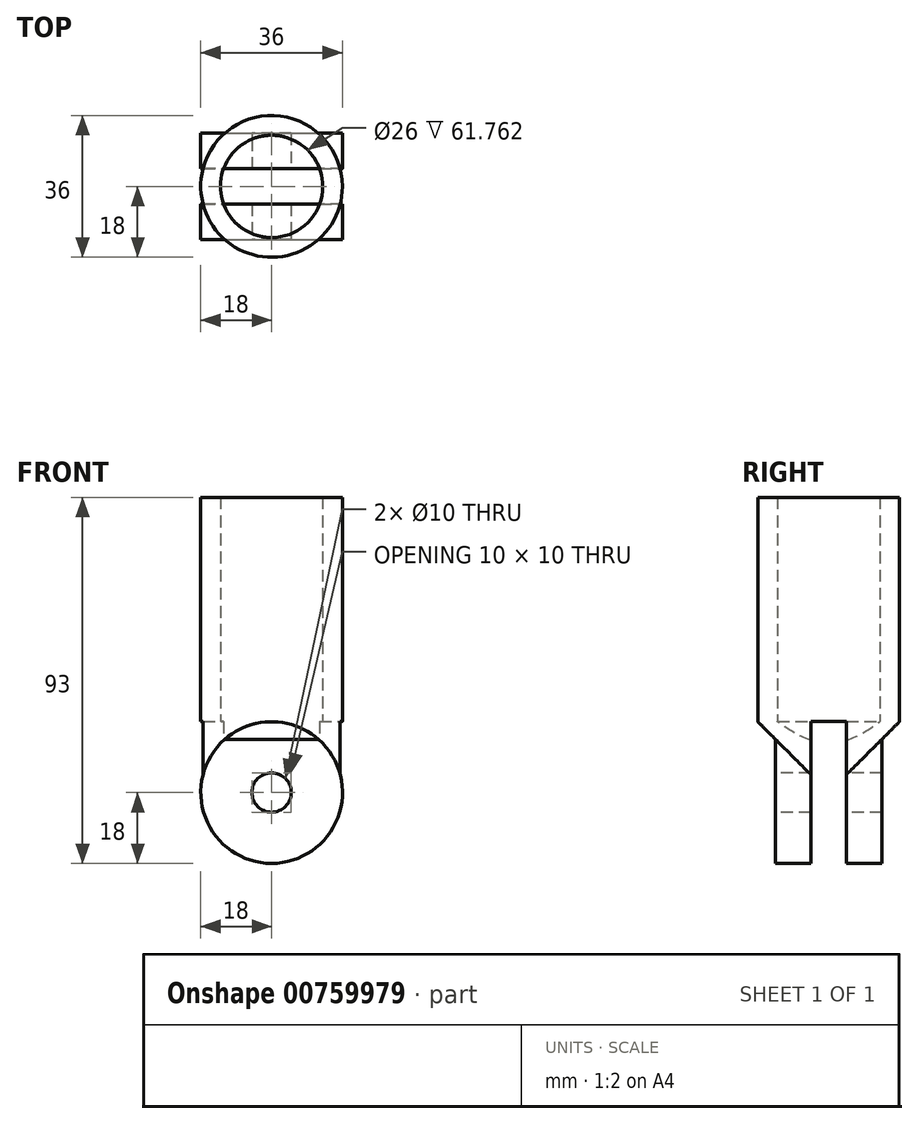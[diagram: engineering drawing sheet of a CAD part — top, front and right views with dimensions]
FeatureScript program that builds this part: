
annotation { "Feature Type Name" : "Feature", "Feature Type Description" : "" }
export const myFeature = defineFeature(function(context is Context, id is Id, definition is map)
    precondition{}
    {
        {
            var Q0;
            Q0=qCreatedBy(makeId("Top.planeOp"),FACE);
            var sketch = newSketch(context, id + "F0", { "sketchPlane" : qUnion([Q0])});
            skCircle(sketch, "E0", {"center": v(0, 0) * mm, "radius": 18 * mm});
            skCircle(sketch, "E1", {"center": v(0, 0) * mm, "radius": 13 * mm});
            skSolve(sketch);
        }
        {
            var Q0;
            Q0 = qSketchRegion(id + "F0", true);
            extrude(context, id + "F1", {"entities" : qUnion([Q0]), "depth" : 75 * mm, "offsetDistance" : 25 * mm});
        }
        {
            var Q0;
            Q0=qCreatedBy(makeId("Front.planeOp"),FACE);
            var sketch = newSketch(context, id + "F2", { "sketchPlane" : qUnion([Q0])});
            skCircle(sketch, "E2", {"center": v(0, 0) * mm, "radius": 18 * mm});
            skSolve(sketch);
        }
        {
            var Q0;
            Q0=makeQuery(id+"F2.imprint","IMPRINT",FACE,{"disambiguationData":[TD([[makeQuery(id+"F2.imprint","IMPRINT",EDGE,{"derivedFrom":sQuery(id+"F2.wireOp",EDGE,"E2")}),1.0]])]});
            extrude(context, id + "F3", {"entities" : qUnion([Q0]), "operationType" : NewBodyOperationType.ADD, "endBound" : BoundingType.SYMMETRIC, "depth" : (9 * 3) * mm, "offsetDistance" : 25 * mm});
        }
        {
            var Q0;
            Q0=qCreatedBy(makeId("Right.planeOp"),FACE);
            var sketch = newSketch(context, id + "F4", { "sketchPlane" : qUnion([Q0])});
            skLineSegment(sketch, "E3.bottom", {"start": v(4.5, -18) * mm, "end": v(-4.5, -18) * mm});
            skLineSegment(sketch, "E3.top", {"start": v(4.5, 18) * mm, "end": v(-4.5, 18) * mm});
            skLineSegment(sketch, "E3.left", {"start": v(4.5, -18) * mm, "end": v(4.5, 18) * mm});
            skLineSegment(sketch, "E3.right", {"start": v(-4.5, -18) * mm, "end": v(-4.5, 18) * mm});
            skPoint(sketch, "E3.middle", {"position": v(0, 0) * mm});
            skSolve(sketch);
        }
        {
            var Q0;
            Q0 = qSketchRegion(id + "F4", true);
            extrude(context, id + "F5", {"entities" : qUnion([Q0]), "operationType" : NewBodyOperationType.REMOVE, "endBound" : BoundingType.SYMMETRIC, "oppositeDirection" : true, "depth" : 40 * mm, "offsetDistance" : 25 * mm});
        }
        {
            var Q0;
            Q0=qCreatedBy(makeId("Front.planeOp"),FACE);
            var sketch = newSketch(context, id + "F6", { "sketchPlane" : qUnion([Q0])});
            skCircle(sketch, "E4", {"center": v(0, 0) * mm, "radius": 5 * mm});
            skSolve(sketch);
        }
        {
            var Q0;
            Q0 = qSketchRegion(id + "F6", true);
            extrude(context, id + "F7", {"entities" : qUnion([Q0]), "operationType" : NewBodyOperationType.REMOVE, "endBound" : BoundingType.SYMMETRIC, "oppositeDirection" : true, "depth" : 40 * mm, "offsetDistance" : 25 * mm});
        }
        {
            var Q0;
            Q0=qCreatedBy(makeId("Right.planeOp"),FACE);
            var sketch = newSketch(context, id + "F8", { "sketchPlane" : qUnion([Q0])});
            skLineSegment(sketch, "E5.0", {"start": v(-4.5, 4.5) * mm, "end": v(-13.5, 13.5) * mm, "construction": true});
            skLineSegment(sketch, "E6.0", {"start": v(-13.5, 13.5) * mm, "end": v(-13.5, -18) * mm, "construction": true});
            skLineSegment(sketch, "E7", {"start": v(-13.5, 0) * mm, "end": v(-13.5, 13.5) * mm});
            skLineSegment(sketch, "E8", {"start": v(-13.5, 13.5) * mm, "end": v(-19.37, 19.37) * mm});
            skLineSegment(sketch, "E9", {"start": v(-19.37, 19.37) * mm, "end": v(-19.37, 0) * mm});
            skLineSegment(sketch, "E10", {"start": v(-19.37, 0) * mm, "end": v(-13.5, 0) * mm});
            skLineSegment(sketch, "E11", {"start": v(-13.5, 13.5) * mm, "end": v(-13.5, 0) * mm});
            skLineSegment(sketch, "E12.MirrorCS", {"start": v(13.5, 0) * mm, "end": v(13.5, 13.5) * mm});
            skLineSegment(sketch, "E13.MirrorCS", {"start": v(13.5, 13.5) * mm, "end": v(13.5, 0) * mm});
            skLineSegment(sketch, "E14.MirrorCS", {"start": v(19.37, 19.37) * mm, "end": v(19.37, 0) * mm});
            skLineSegment(sketch, "E15.MirrorCS", {"start": v(19.37, 0) * mm, "end": v(13.5, 0) * mm});
            skLineSegment(sketch, "E16.MirrorCS", {"start": v(13.5, 13.5) * mm, "end": v(19.37, 19.37) * mm});
            skSolve(sketch);
        }
        {
            var Q0;
            Q0 = qSketchRegion(id + "F8", true);
            extrude(context, id + "F9", {"entities" : qUnion([Q0]), "operationType" : NewBodyOperationType.REMOVE, "endBound" : BoundingType.SYMMETRIC, "oppositeDirection" : true, "depth" : 29 * mm, "offsetDistance" : 25 * mm});
        }
    });
